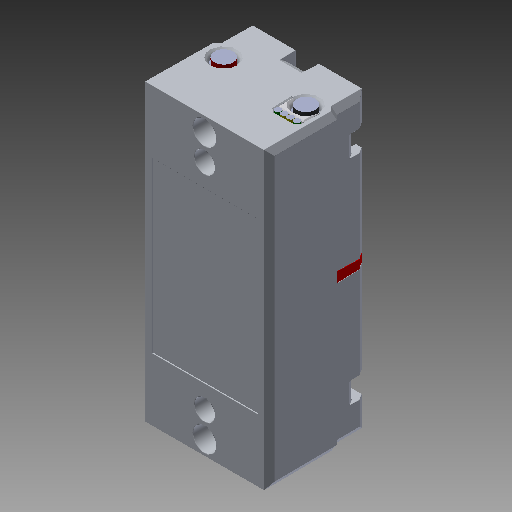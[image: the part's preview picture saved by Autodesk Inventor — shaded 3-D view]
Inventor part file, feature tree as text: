
AUTODESK INVENTOR PART (.ipt)
format: ipt  version: 2019 (Build 230136000, 136)  size: 3,560,448 bytes
history: native  units: in
note: dims shown in document units (in); Inventor stores cm internally (conversion verified against a paired STEP export)
features: boolean_combine x1, other x1, extrude x1, imported_body x1, sketch x1
ambient origin geometry x8: Origin, YZ Plane, XZ Plane, XY Plane, X Axis, Y Axis, Z Axis, Center Point
bodies: Body1 (feature_tree)
feature tree (5):
  boolean_combine  "Combine11"
  other  "Talon SRX1"
  extrude  "Extrusion1"  [1 undecoded]
  imported_body  "Base1"
  sketch  "Sketch1"  dims[d0=3.937in d1=0.0in]
note: 1 required parameter value undecoded (feature->parameter linkage not recoverable at this tier; creation-order binding heuristic only, values carry confidence <= 0.55)
